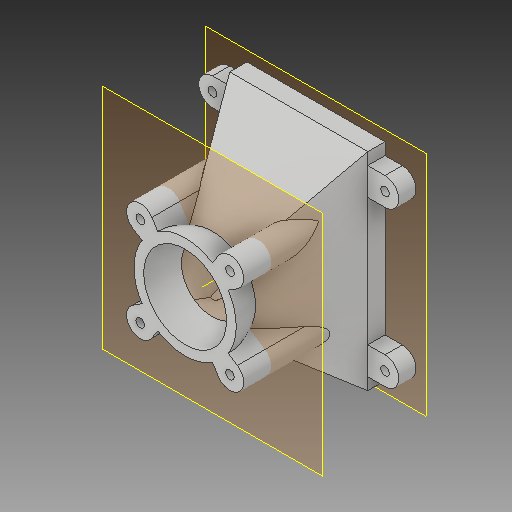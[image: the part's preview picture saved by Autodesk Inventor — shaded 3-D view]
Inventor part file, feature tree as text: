
AUTODESK INVENTOR PART (.ipt)
format: ipt  version: 2017 (Build 210142000, 142)  size: 523,776 bytes
history: native  units: mm
features: sketch x6, other x6, extrude x3, reference x3, projected_geometry x3, plane x2, loft x2, revolve x1, pattern_circular x1
ambient origin geometry x8: Origin, YZ Plane, XZ Plane, XY Plane, X Axis, Y Axis, Z Axis, Center Point
bodies: Solid1 (feature_tree)
feature tree (27):
  plane  "Work Plane1"
  extrude  "Extrusion1"  Depth=25.0mm
  plane  "Work Plane2"
  sketch  "Sketch2"  dims[d3=25.0mm d4=18.0mm]
  sketch  "Sketch3"  dims[d5=0.0mm d6=90.0deg d7=0.0mm d8=90.0deg]
  other  "Work Axis1"
  loft  "Loft1"
  loft  "Loft2"
  revolve  "Revolution1"  Angle=90.0deg
  extrude  "Extrusion2"  TaperAngle=90.0deg  [1 undecoded]
  pattern_circular  "Circular Pattern1"  [2 undecoded]
  extrude  "Extrusion3"  Depth=5.0mm
  sketch  "Sketch1"  dims[d0=5.0mm d1=0.0mm d2=25.0mm]
  reference  "Reference1"
  projected_geometry  "Projected Loop1"
  sketch  "Sketch4"  dims[d9=0.0mm d10=90.0deg d11=0.0mm d12=90.0deg]
  sketch  "Sketch5"  dims[d13=12.0mm d14=90.0deg]
  projected_geometry  "Projected Loop2"
  sketch  "Sketch6"  dims[d15=26.0mm d16=26.0mm d17=2.5mm d18=4.0mm d19=5.0mm d20=0.0mm d21=40.0mm d22=360.0deg d24=25.0mm d25=8.0mm d26=10.0mm d27=10.0mm d28=5.0mm d29=0.0mm]
  projected_geometry  "Projected Loop3"
  reference  "Reference2"
  reference  "Reference3"
  parser-record x1  (decoder bookkeeping rows leaked as tree rows — omitted from the tree; the rows remain in map.json)
  other  "gearbox.iam"
  other  "shifter box 1:1"
  other  "long selector:1"
  other  "short selector:1"
note: 3 required parameter values undecoded (feature->parameter linkage not recoverable at this tier; creation-order binding heuristic only, values carry confidence <= 0.55)
note: 1 file-system path scrubbed to <path> (originals preserved in map.json)
